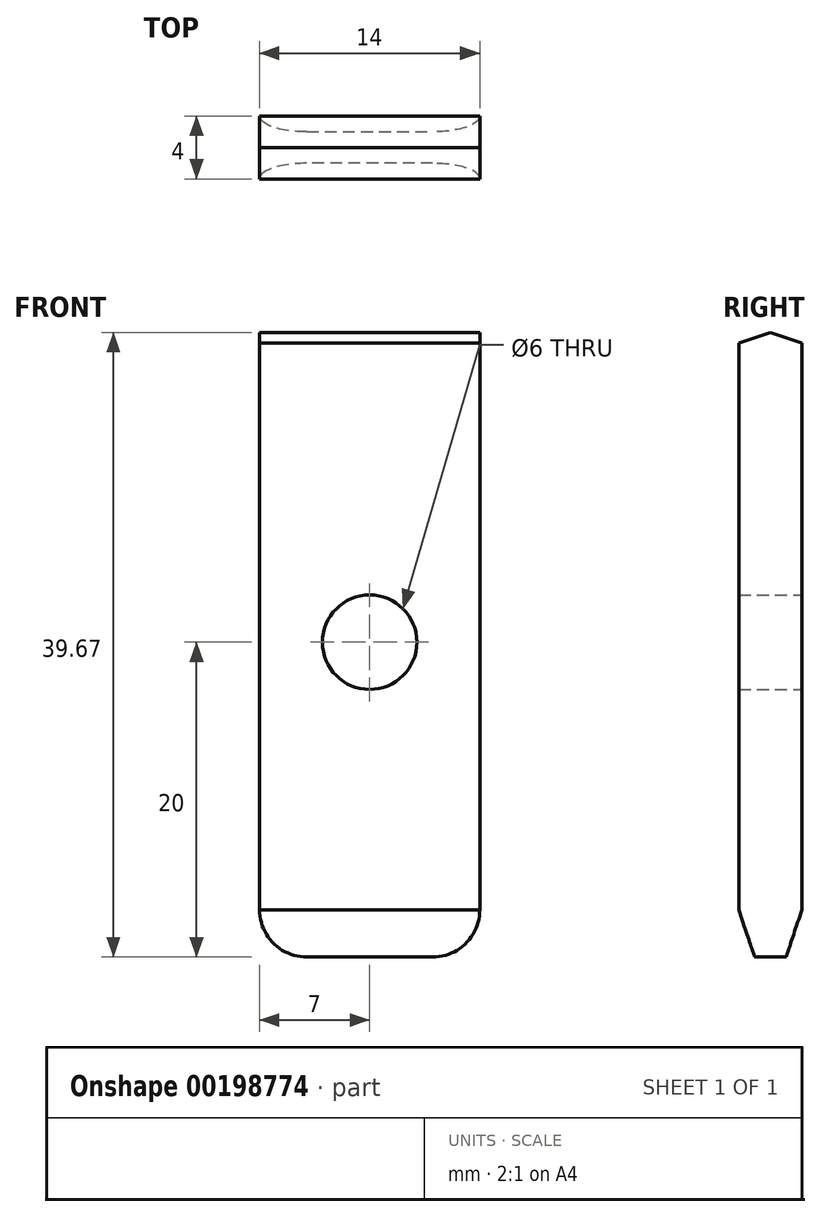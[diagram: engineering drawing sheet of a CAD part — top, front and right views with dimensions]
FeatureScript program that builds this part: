
annotation { "Feature Type Name" : "Feature", "Feature Type Description" : "" }
export const myFeature = defineFeature(function(context is Context, id is Id, definition is map)
    precondition{}
    {
        {
            var Q0;
            Q0=qCreatedBy(makeId("Front.planeOp"),FACE);
            var sketch = newSketch(context, id + "F0", { "sketchPlane" : qUnion([Q0])});
            skLineSegment(sketch, "E0.bottom", {"start": v(7, 20) * mm, "end": v(-7, 20) * mm});
            skLineSegment(sketch, "E0.top", {"start": v(7, -20) * mm, "end": v(-7, -20) * mm});
            skLineSegment(sketch, "E0.left", {"start": v(7, 20) * mm, "end": v(7, -20) * mm});
            skLineSegment(sketch, "E0.right", {"start": v(-7, 20) * mm, "end": v(-7, -20) * mm});
            skPoint(sketch, "E0.middle", {"position": v(0, 0) * mm});
            skCircle(sketch, "E1", {"center": v(0, 0) * mm, "radius": 3 * mm});
            skSolve(sketch);
        }
        {
            var Q0;
            Q0 = qSketchRegion(id + "F0", true);
            extrude(context, id + "F1", {"entities" : qUnion([Q0]), "depth" : 4 * mm, "symmetric" : true});
        }
        {
            var Q0;
            Q0=makeQuery(id+"F1.opExtrude","CAP_EDGE",EDGE,{"disambiguationData":[OSD([sQuery(id+"F0.wireOp",EDGE,"E0.bottom")])],"isStart":false});
            var Q1;
            Q1=makeQuery(id+"F1.opExtrude","CAP_EDGE",EDGE,{"disambiguationData":[OSD([sQuery(id+"F0.wireOp",EDGE,"E0.bottom")])],"isStart":true});
            var Q2;
            Q2=makeQuery(id+"F1.opExtrude","CAP_EDGE",EDGE,{"disambiguationData":[OSD([sQuery(id+"F0.wireOp",EDGE,"E0.top")])],"isStart":false});
            var Q3;
            Q3=makeQuery(id+"F1.opExtrude","CAP_EDGE",EDGE,{"disambiguationData":[OSD([sQuery(id+"F0.wireOp",EDGE,"E0.top")])],"isStart":true});
            chamfer(context, id + "F2", {"entities" : qUnion([Q0, Q1, Q2, Q3]), "chamferType" : ChamferType.TWO_OFFSETS, "width1" : 3 * mm, "oppositeDirection" : false, "width2" : 1 * mm, "tangentPropagation" : true});
        }
        {
            var Q0;
            Q0=makeQuery(id+"F1.opExtrude","SWEPT_EDGE",EDGE,{"disambiguationData":[OSD([sQuery(id+"F0.wireOp",EDGE,"E0.bottom"),sQuery(id+"F0.wireOp",EDGE,"E0.left")])]});
            var Q1;
            Q1=makeQuery(id+"F1.opExtrude","SWEPT_EDGE",EDGE,{"disambiguationData":[OSD([sQuery(id+"F0.wireOp",EDGE,"E0.bottom"),sQuery(id+"F0.wireOp",EDGE,"E0.right")])]});
            var Q2;
            Q2=makeQuery(id+"F1.opExtrude","SWEPT_EDGE",EDGE,{"disambiguationData":[OSD([sQuery(id+"F0.wireOp",EDGE,"E0.top"),sQuery(id+"F0.wireOp",EDGE,"E0.left")])]});
            var Q3;
            Q3=makeQuery(id+"F1.opExtrude","SWEPT_EDGE",EDGE,{"disambiguationData":[OSD([sQuery(id+"F0.wireOp",EDGE,"E0.top"),sQuery(id+"F0.wireOp",EDGE,"E0.right")])]});
            fillet(context, id + "F3", {"entities" : qUnion([Q0, Q1, Q2, Q3]), "radius" : 3 * mm, "tangentPropagation" : true, "allowEdgeOverflow" : false});
        }
    });
